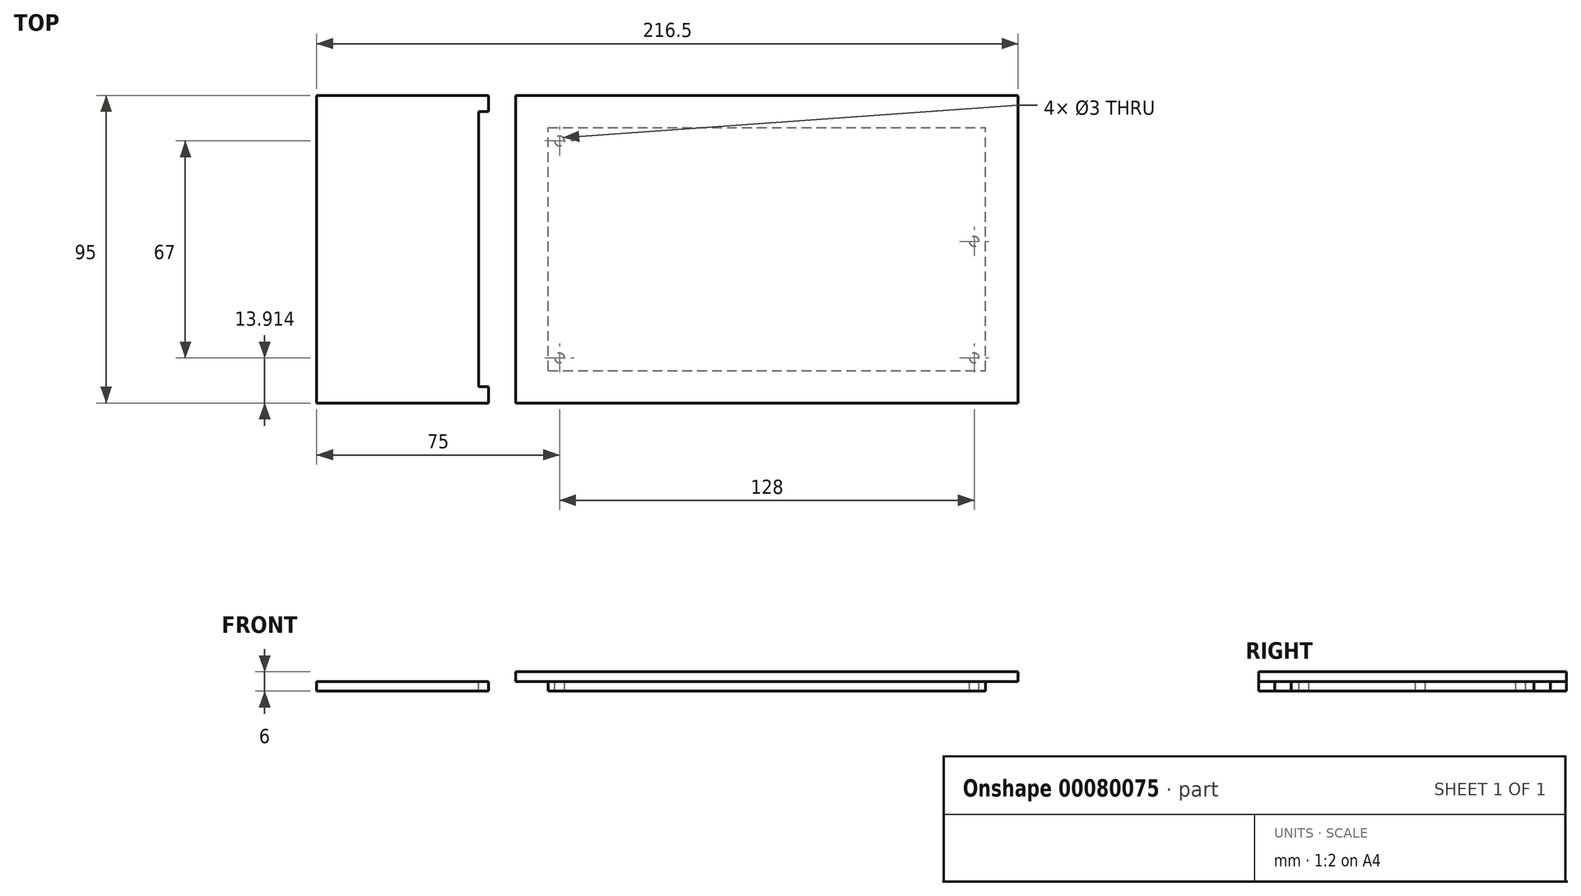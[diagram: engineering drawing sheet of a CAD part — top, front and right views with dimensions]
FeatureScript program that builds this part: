
annotation { "Feature Type Name" : "Feature", "Feature Type Description" : "" }
export const myFeature = defineFeature(function(context is Context, id is Id, definition is map)
    precondition{}
    {
        {
            var Q0;
            Q0=qCreatedBy(makeId("Top.planeOp"),FACE);
            var sketch = newSketch(context, id + "F0", { "sketchPlane" : qUnion([Q0])});
            skLineSegment(sketch, "E0.bottom", {"start": v(0, 0) * mm, "end": v(135, 0) * mm});
            skLineSegment(sketch, "E0.top", {"start": v(0, 75) * mm, "end": v(135, 75) * mm});
            skLineSegment(sketch, "E0.left", {"start": v(0, 0) * mm, "end": v(0, 75) * mm});
            skLineSegment(sketch, "E0.right", {"start": v(135, 0) * mm, "end": v(135, 75) * mm});
            skSolve(sketch);
        }
        {
            var Q0;
            Q0=makeQuery(id+"F0.imprint","IMPRINT",FACE,{"disambiguationData":[TD([[makeQuery(id+"F0.imprint","IMPRINT",EDGE,{"derivedFrom":sQuery(id+"F0.wireOp",EDGE,"E0.bottom")}),1.0]])]});
            extrude(context, id + "F1", {"entities" : qUnion([Q0]), "depth" : 3 * mm});
        }
        {
            var Q0;
            Q0=makeQuery(id+"F1.opExtrude","CAP_FACE",FACE,{"disambiguationData":[OSD([sQuery(id+"F0.wireOp",EDGE,"E0.bottom"),sQuery(id+"F0.wireOp",EDGE,"E0.top"),sQuery(id+"F0.wireOp",EDGE,"E0.left"),sQuery(id+"F0.wireOp",EDGE,"E0.right")])],"isStart":false});
            var sketch = newSketch(context, id + "F2", { "sketchPlane" : qUnion([Q0])});
            skCircle(sketch, "E1", {"center": v(3.5, 70.91) * mm, "radius": 1.5 * mm});
            skCircle(sketch, "E2", {"center": v(3.5, 3.91) * mm, "radius": 1.5 * mm});
            skCircle(sketch, "E3", {"center": v(131.5, 3.91) * mm, "radius": 1.5 * mm});
            skCircle(sketch, "E4", {"center": v(131.5, 39.91) * mm, "radius": 1.5 * mm});
            skLineSegment(sketch, "E5", {"start": v(3.5, 3.91) * mm, "end": v(0, 3.91) * mm, "construction": true});
            skLineSegment(sketch, "E6", {"start": v(131.5, 3.91) * mm, "end": v(131.5, 0) * mm, "construction": true});
            skLineSegment(sketch, "E7", {"start": v(135, 3.91) * mm, "end": v(131.5, 3.91) * mm, "construction": true});
            skSolve(sketch);
        }
        {
            var Q0;
            Q0 = qSketchRegion(id + "F2", true);
            extrude(context, id + "F3", {"entities" : qUnion([Q0]), "operationType" : NewBodyOperationType.REMOVE, "oppositeDirection" : true, "depth" : 25 * mm});
        }
        {
            var Q0;
            Q0=makeQuery(id+"F1.opExtrude","CAP_FACE",FACE,{"disambiguationData":[OSD([sQuery(id+"F0.wireOp",EDGE,"E0.bottom"),sQuery(id+"F0.wireOp",EDGE,"E0.top"),sQuery(id+"F0.wireOp",EDGE,"E0.left"),sQuery(id+"F0.wireOp",EDGE,"E0.right")])],"isStart":false});
            var sketch = newSketch(context, id + "F4", { "sketchPlane" : qUnion([Q0])});
            skLineSegment(sketch, "E8.bottom", {"start": v(-10, 85) * mm, "end": v(145, 85) * mm});
            skLineSegment(sketch, "E8.top", {"start": v(-10, -10) * mm, "end": v(145, -10) * mm});
            skLineSegment(sketch, "E8.left", {"start": v(-10, 85) * mm, "end": v(-10, -10) * mm});
            skLineSegment(sketch, "E8.right", {"start": v(145, 85) * mm, "end": v(145, -10) * mm});
            skSolve(sketch);
        }
        {
            var Q0;
            Q0 = qSketchRegion(id + "F4", true);
            extrude(context, id + "F5", {"entities" : qUnion([Q0]), "depth" : 3 * mm});
        }
        {
            var Q0;
            Q0=makeQuery(id+"F5.opExtrude","CAP_FACE",FACE,{"disambiguationData":[OSD([sQuery(id+"F4.wireOp",EDGE,"E8.bottom"),sQuery(id+"F4.wireOp",EDGE,"E8.top"),sQuery(id+"F4.wireOp",EDGE,"E8.left"),sQuery(id+"F4.wireOp",EDGE,"E8.right")])],"isStart":true});
            var sketch = newSketch(context, id + "F6", { "sketchPlane" : qUnion([Q0])});
            skLineSegment(sketch, "E9.bottom", {"start": v(-21.5, 10) * mm, "end": v(-71.5, 10) * mm});
            skLineSegment(sketch, "E9.top", {"start": v(-21.5, -85) * mm, "end": v(-71.5, -85) * mm});
            skLineSegment(sketch, "E9.left", {"start": v(-21.5, 5) * mm, "end": v(-21.5, -80) * mm});
            skLineSegment(sketch, "E9.right", {"start": v(-71.5, 10) * mm, "end": v(-71.5, -85) * mm});
            skLineSegment(sketch, "E10.bottom", {"start": v(-21.5, 10) * mm, "end": v(-18.5, 10) * mm});
            skLineSegment(sketch, "E10.top", {"start": v(-21.5, 5) * mm, "end": v(-18.5, 5) * mm});
            skLineSegment(sketch, "E10.right", {"start": v(-18.5, 10) * mm, "end": v(-18.5, 5) * mm});
            skLineSegment(sketch, "E11.bottom", {"start": v(-21.5, -85) * mm, "end": v(-18.5, -85) * mm});
            skLineSegment(sketch, "E11.top", {"start": v(-21.5, -80) * mm, "end": v(-18.5, -80) * mm});
            skLineSegment(sketch, "E11.right", {"start": v(-18.5, -85) * mm, "end": v(-18.5, -80) * mm});
            skSolve(sketch);
        }
        {
            var Q0;
            Q0=makeQuery(id+"F6.imprint","IMPRINT",FACE,{"disambiguationData":[TD([[makeQuery(id+"F6.imprint","IMPRINT",EDGE,{"derivedFrom":sQuery(id+"F6.wireOp",EDGE,"E9.bottom")}),1.0]])]});
            extrude(context, id + "F7", {"entities" : qUnion([Q0]), "depth" : 3 * mm});
        }
    });
